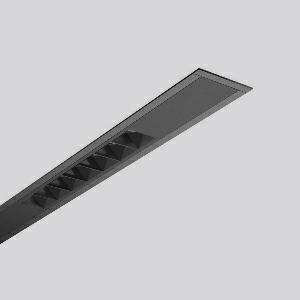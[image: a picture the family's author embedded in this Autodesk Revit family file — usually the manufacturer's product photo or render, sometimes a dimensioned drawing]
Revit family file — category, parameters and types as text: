
# Revit family: less_is_more_beamline_312477_003_1_0d36
name_source: partatom
category: Lighting Fixtures
units: mm (PartAtom-declared; Revit-internal decimal feet)

## family parameters
Cut with Voids When Loaded = No
Host = Face
Light Source = No
Part Type = Normal
Room Calculation Point = No
Round Connector Dimension = Use Diameter
Shared = No

## types (1)
- LESS IS MORE BEAMLINE (1 x LED Modul 940, 1087.5 lm, 4000)
    Apparent Load = 47 VA
    CIE Flux Codes = 100 100 100 100 100
    Color Rendering = 92
    Color Temperature = 4000
    Default Elevation = 1800 mm
    Description = Series: LESS IS MORE BEAMLINE
Linear recessed ceiling and wall luminaire for aesthetically sophisticated lighting. Luminaire with four LED light units. Housing: extruded aluminium profile, powder-coated. End cap aluminium powder-coated. LED light unit with MRS technology: Mini-Reflector-System made of metallised thermoplastic with prismatic black glare-suppressing frame for pleasant glare-free light (RUG < 10). Each LED light unit has 7 reflector elements. Narrow beam light distribution. Ceiling installation with pre-assembled SBS mounting system. LED unit with integrated converter interchangeable and removable. Suitable for through-wiring. 
Colour: deep black, matt (RAL 9005)
Length: 2262 mm
Width: 71 mm
Height: 1.5 mm
Cut-out length: 2243 mm
Cut-out width: 60 mm
Recess height: 125 mm
Luminaire: recess height: 106 mm
Lamp: LED
Socket: without socket
Colour temperature: 4000K
Colour rendering index (CRI): 90
System power: 47 W
Rated luminous flux: 4350 lm
Luminous efficiency: 93 lm/W
Control gear: Regulated power supply
Protection class: I
Type of protection: IP 20
    Height = 0 mm  [stored 0 ft]
    Lamp = 1 x LED Modul 940
    Lamp Light Flux = 1087.5 lm
    Lamp count = 1
    Length = 2262 mm
    Lifetime = 50000 h
    Luminous efficacy = 93 lm/W
    Manufacturer = RZB
    ModVariant = No
    Model = 312477.003.1
    Mounting Place = Ceiling, Wall
    Mounting Type = Recessed
    Number of Poles = 1
    OnlyDefault = Yes
    Power Factor = 1
    Product Name = LESS IS MORE BEAMLINE
    Product group = Recessed LED linear luminaires
    ProductGroupID = 407
    Protection Class = Protection class I
    Protection Degree = IP 20
    RLX_Detail_Level = 1
    RLX_Emergency_Light_Flux = 0 lm
    RLX_Emergency_Type = 0
    RLX_Emergency_Type_DB = No
    RlxData = <blob elided: 24653 chars, md5=e7ba2765>
    Socket = socket
    Standby Power = 0 W
    System Light Flux = 4350 lm
    System Power = 47 W
    Type Comments = Product without accessories
    Type Image = 312465.003.jpg
    URL = http://relux.com
    VarID = ---
    Voltage = 230 V
    Voltage Range = 220-240 V
    Weight = 0.00 kg
    Width = 71 mm

note: [stored X ft] marks values corroborated as IEEE doubles in the binary element streams (Revit-internal decimal feet)

## geometry (parser evidence)
native form markers: Blend x4, Sweep x19
no freeform markers — native parametric forms only
